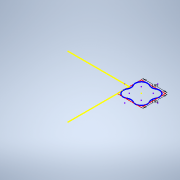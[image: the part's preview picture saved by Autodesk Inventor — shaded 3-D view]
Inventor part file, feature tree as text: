
AUTODESK INVENTOR PART (.ipt)
format: ipt  version: 2021 (Build 250183000, 183)  size: 93,696 bytes
history: native  units: in
note: dims shown in document units (in); Inventor stores cm internally (conversion verified against a paired STEP export)
features: sketch x1
ambient origin geometry x8: Origin, YZ Plane, XZ Plane, XY Plane, X Axis, Y Axis, Z Axis, Center Point
feature tree (1):
  sketch  "Boceto2"  dims[d7=7.6772in d8=7.6772in]
